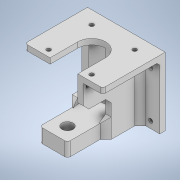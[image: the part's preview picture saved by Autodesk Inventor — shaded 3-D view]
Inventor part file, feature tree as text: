
AUTODESK INVENTOR PART (.ipt)
format: ipt  version: 2022 (Build 260153000, 153)  size: 527,360 bytes
history: native  units: mm
features: sketch x14, extrude x13, chamfer x4, hole x3, other x1, fillet x1
ambient origin geometry x8: Origin, YZ Plane, XZ Plane, XY Plane, X Axis, Y Axis, Z Axis, Center Point
bodies: Body1 (feature_tree)
feature tree (36):
  other  "Sólido1"
  sketch  "Esboço1"  dims[d0=56.0mm d1=10.0mm]
  extrude  "Extrusão1"  Depth=10.0mm
  extrude  "Extrusão2"  Depth=4.0mm TaperAngle=0.0deg
  hole  "Furo1"  [1 undecoded]
  hole  "Furo2"  [1 undecoded]
  extrude  "Extrusão3"  Depth=22.0mm
  extrude  "Extrusão4"  Depth=15.5mm
  sketch  "Esboço6"  dims[d25=25.0mm d26=39.0mm d27=0.0mm]
  extrude  "Extrusão5"  Depth=20.0mm
  extrude  "Extrusão6"  Depth=3.0mm
  extrude  "Extrusão7"  Depth=3.0mm
  extrude  "Extrusão8"  Depth=20.0mm TaperAngle=0.0deg
  extrude  "Extrusão9"  Depth=14.0mm TaperAngle=0.0deg
  extrude  "Extrusão10"  Depth=14.0mm TaperAngle=0.0deg
  chamfer  "Chanfro2"  Distance=39.0mm
  fillet  "Arredondamento1"  Radius=10.0mm
  hole  "Furo3"  [1 undecoded]
  chamfer  "Chanfro3"  Distance=2.0mm
  extrude  "Extrusão11"  Depth=33.0mm
  extrude  "Extrusão12"  Depth=4.0mm TaperAngle=45.0deg
  chamfer  "Chanfro4"  Distance=2.5mm
  extrude  "Extrusão14"  Depth=4.0mm
  chamfer  "Chanfro5"  Distance=5.0mm
  sketch  "Esboço2"  dims[d2=20.0mm d3=4.0mm d4=0.0mm]
  sketch  "Esboço3"  dims[d5=52.426mm d6=0.0mm]
  sketch  "Esboço4"  dims[d10=8.0mm d11=6.0mm d12=4.0mm d13=2.0mm d14=90.0deg d15=8.0mm d16=20.594885mm]
  sketch  "Esboço5"  dims[d17=3.0mm d18=6.0mm d19=4.0mm d20=2.0mm d21=90.0deg d22=8.0mm d23=20.594885mm d24=10.0mm]
  sketch  "Esboço7"  dims[d28=22.0mm d29=0.0mm d30=15.5mm]
  sketch  "Esboço8"  dims[d31=15.5mm d32=15.5mm]
  sketch  "Esboço9"  dims[d33=15.5mm d34=20.0mm]
  sketch  "Esboço10"  dims[d35=0.0mm d36=0.0mm d37=3.0mm]
  sketch  "Esboço11"  dims[d38=3.0mm d39=3.0mm]
  sketch  "Esboço12"  dims[d40=3.0mm d41=20.0mm d42=0.0mm]
  sketch  "Esboço13"  dims[d43=4.0mm d44=14.0mm d45=0.0mm]
  sketch  "Esboço15"  dims[d46=4.0mm d47=14.0mm d48=0.0mm d49=39.0mm d50=0.0mm d51=10.0mm d52=0.0mm d53=4.0mm d54=2.0mm d55=45.0deg d56=2.0mm d57=33.0mm d58=3.0mm d59=6.0mm d60=4.0mm d61=2.0mm d62=90.0deg d63=8.0mm d64=20.594885mm d65=4.0mm d66=2.0mm d67=45.0deg d68=2.5mm d69=4.0mm d70=5.0mm d71=2.5mm d72=4.0mm d73=5.0mm d74=2.0mm d75=0.0mm d76=2.5mm d77=4.0mm d78=5.0mm d79=2.5mm d80=4.0mm d81=5.0mm d82=2.0mm d83=0.0mm d84=2.0mm d85=2.0mm d86=45.0deg d87=15.5mm d88=15.5mm d91=10.0mm d92=0.0mm d94=2.0mm d95=2.0mm d96=45.0deg]
note: 3 required parameter values undecoded (feature->parameter linkage not recoverable at this tier; creation-order binding heuristic only, values carry confidence <= 0.55)
